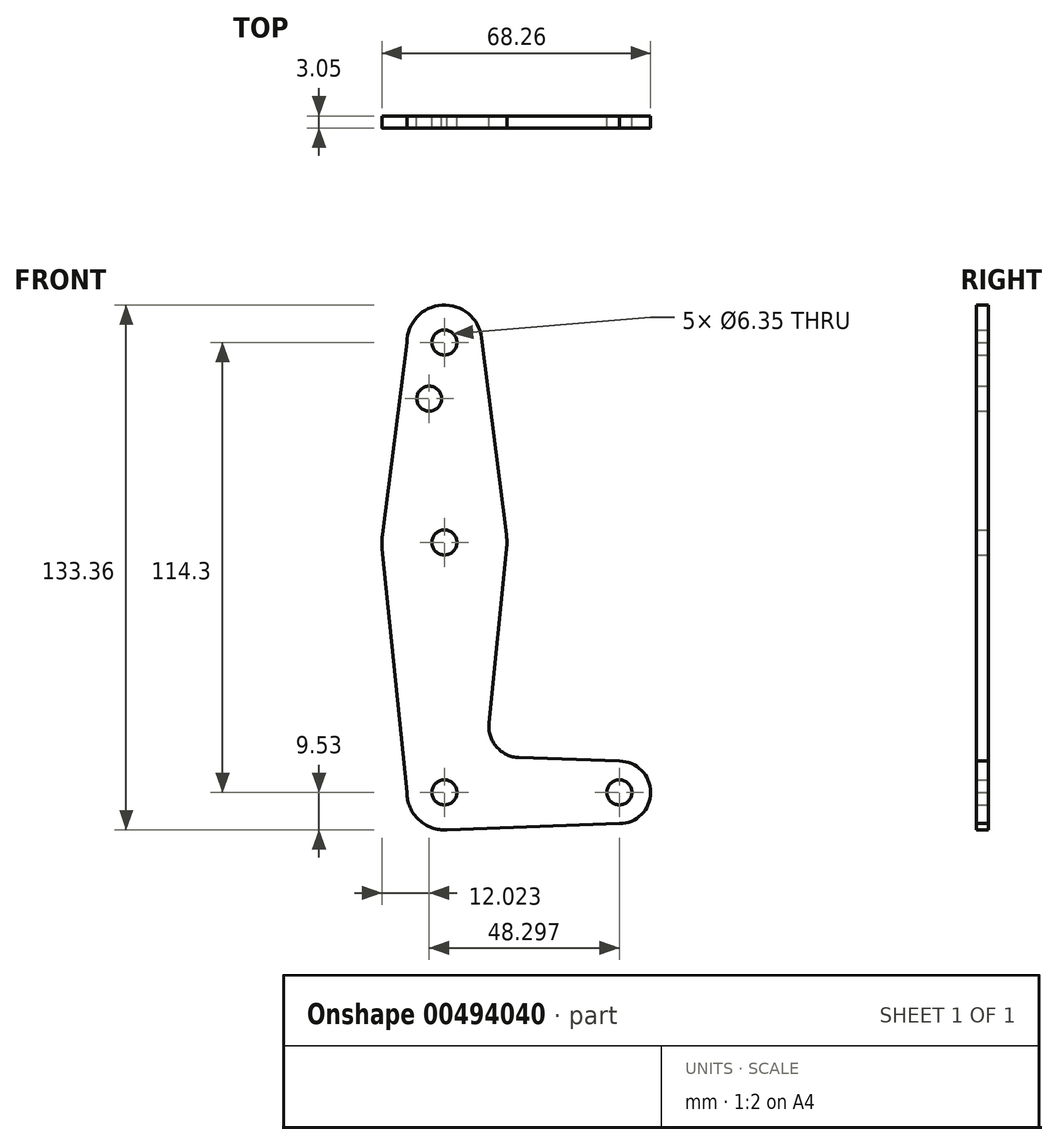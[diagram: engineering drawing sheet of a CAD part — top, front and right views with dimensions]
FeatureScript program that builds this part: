
annotation { "Feature Type Name" : "Feature", "Feature Type Description" : "" }
export const myFeature = defineFeature(function(context is Context, id is Id, definition is map)
    precondition{}
    {
        {
            var Q0;
            Q0=qCreatedBy(makeId("Front.planeOp"),FACE);
            var sketch = newSketch(context, id + "F0", { "sketchPlane" : qUnion([Q0])});
            skLineSegment(sketch, "E0", {"start": v(0, 0) * mm, "end": v(0, 114.3) * mm, "construction": true});
            skLineSegment(sketch, "E1", {"start": v(0, 0) * mm, "end": v(44.45, 0) * mm});
            skCircle(sketch, "E2", {"center": v(0, 114.3) * mm, "radius": 9.53 * mm});
            skCircle(sketch, "E3", {"center": v(0, 63.5) * mm, "radius": 15.88 * mm});
            skCircle(sketch, "E4", {"center": v(0, 0) * mm, "radius": 9.53 * mm});
            skCircle(sketch, "E5", {"center": v(44.45, 0) * mm, "radius": 7.94 * mm});
            skLineSegment(sketch, "E6", {"start": v(0, 0) * mm, "end": v(0, 9.53) * mm});
            skLineSegment(sketch, "E7", {"start": v(0, 0) * mm, "end": v(0, -9.53) * mm});
            skLineSegment(sketch, "E8", {"start": v(0, -9.52) * mm, "end": v(44.45, -7.94) * mm});
            skLineSegment(sketch, "E9", {"start": v(18.95, 8.85) * mm, "end": v(44.45, 7.94) * mm});
            skLineSegment(sketch, "E10", {"start": v(-9.53, 114.3) * mm, "end": v(-15.75, 65.5) * mm});
            skLineSegment(sketch, "E11", {"start": v(9.45, 115.5) * mm, "end": v(15.75, 65.48) * mm});
            skLineSegment(sketch, "E12", {"start": v(-15.8, 61.9) * mm, "end": v(-9.52, 0) * mm});
            skLineSegment(sketch, "E13", {"start": v(11.33, 17.6) * mm, "end": v(15.8, 61.9) * mm});
            skCircle(sketch, "E14", {"center": v(0, 114.3) * mm, "radius": 3.18 * mm});
            skCircle(sketch, "E15", {"center": v(0, 63.5) * mm, "radius": 3.18 * mm});
            skCircle(sketch, "E16", {"center": v(0, 0) * mm, "radius": 3.18 * mm});
            skCircle(sketch, "E17", {"center": v(44.45, 0) * mm, "radius": 3.18 * mm});
            skCircle(sketch, "E18", {"center": v(-3.85, 100.03) * mm, "radius": 3.18 * mm});
            skArc(sketch, "E19.filletArc", {"start": v(11.33, 17.6) * mm, "mid": v(13.25, 11.57) * mm, "end": v(18.95, 8.85) * mm});
            skSolve(sketch);
        }
        {
            var Q0;
            Q0 = qSketchRegion(id + "F0", true);
            var Q1;
            {var subQ0=sQuery(id+"F0.wireOp",EDGE,"E16");var subQ1=sQuery(id+"F0.wireOp",EDGE,"E1");var subQ2=makeQuery(id+"F0.imprint","INTERSECT",VERTEX,{"derivedFrom":[subQ1,subQ0]});Q1=makeQuery(id+"F0.imprint","IMPRINT",FACE,{"disambiguationData":[TD([[makeQuery(id+"F0.imprint","IMPRINT",EDGE,{"disambiguationData":[TD([[subQ2,-1.0]])],"derivedFrom":subQ1}),1.0]])]});}
            extrude(context, id + "F1", {"entities" : qUnion([Q0, Q1]), "depth" : 3.05 * mm});
        }
    });
